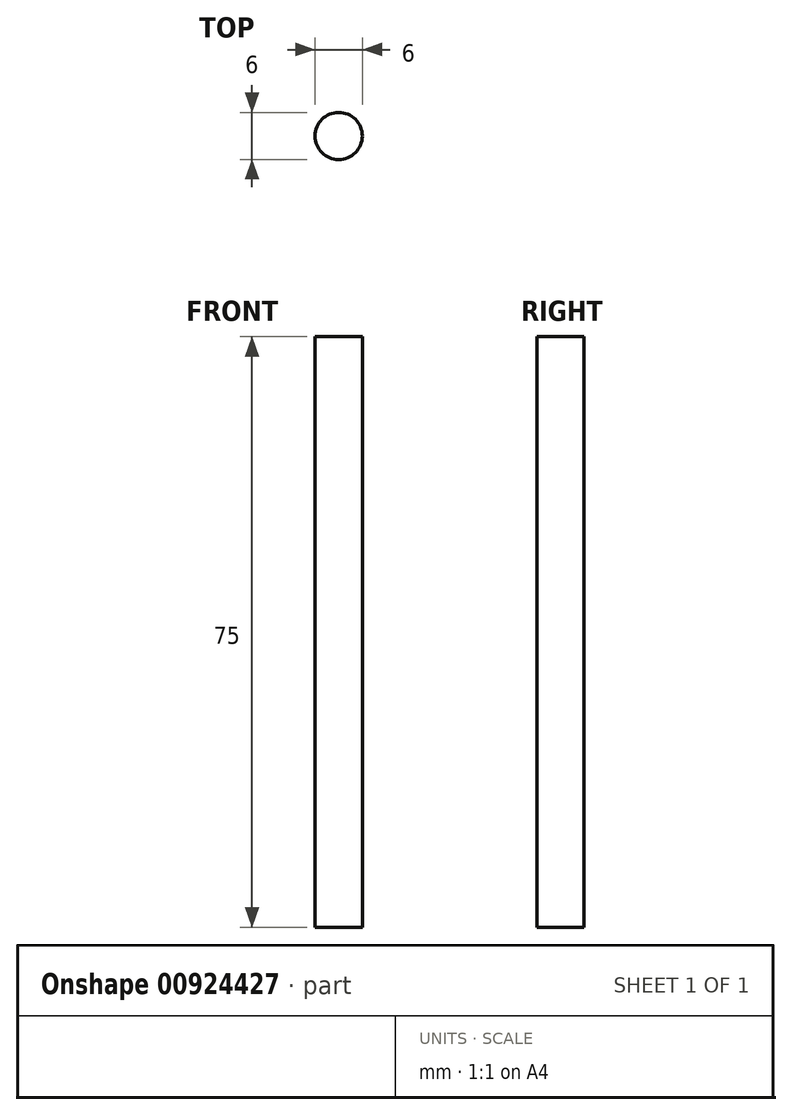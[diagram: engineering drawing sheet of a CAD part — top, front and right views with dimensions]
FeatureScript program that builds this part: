
annotation { "Feature Type Name" : "Feature", "Feature Type Description" : "" }
export const myFeature = defineFeature(function(context is Context, id is Id, definition is map)
    precondition{}
    {
        {
            var Q0;
            Q0=qCreatedBy(makeId("Top.planeOp"),FACE);
            var sketch = newSketch(context, id + "F0", { "sketchPlane" : qUnion([Q0])});
            skCircle(sketch, "E0", {"center": v(-12.07, 22.95) * mm, "radius": 3 * mm});
            skSolve(sketch);
        }
        {
            var Q0;
            Q0 = qSketchRegion(id + "F0", true);
            extrude(context, id + "F1", {"entities" : qUnion([Q0]), "depth" : 75 * mm, "offsetDistance" : 25 * mm});
        }
    });
